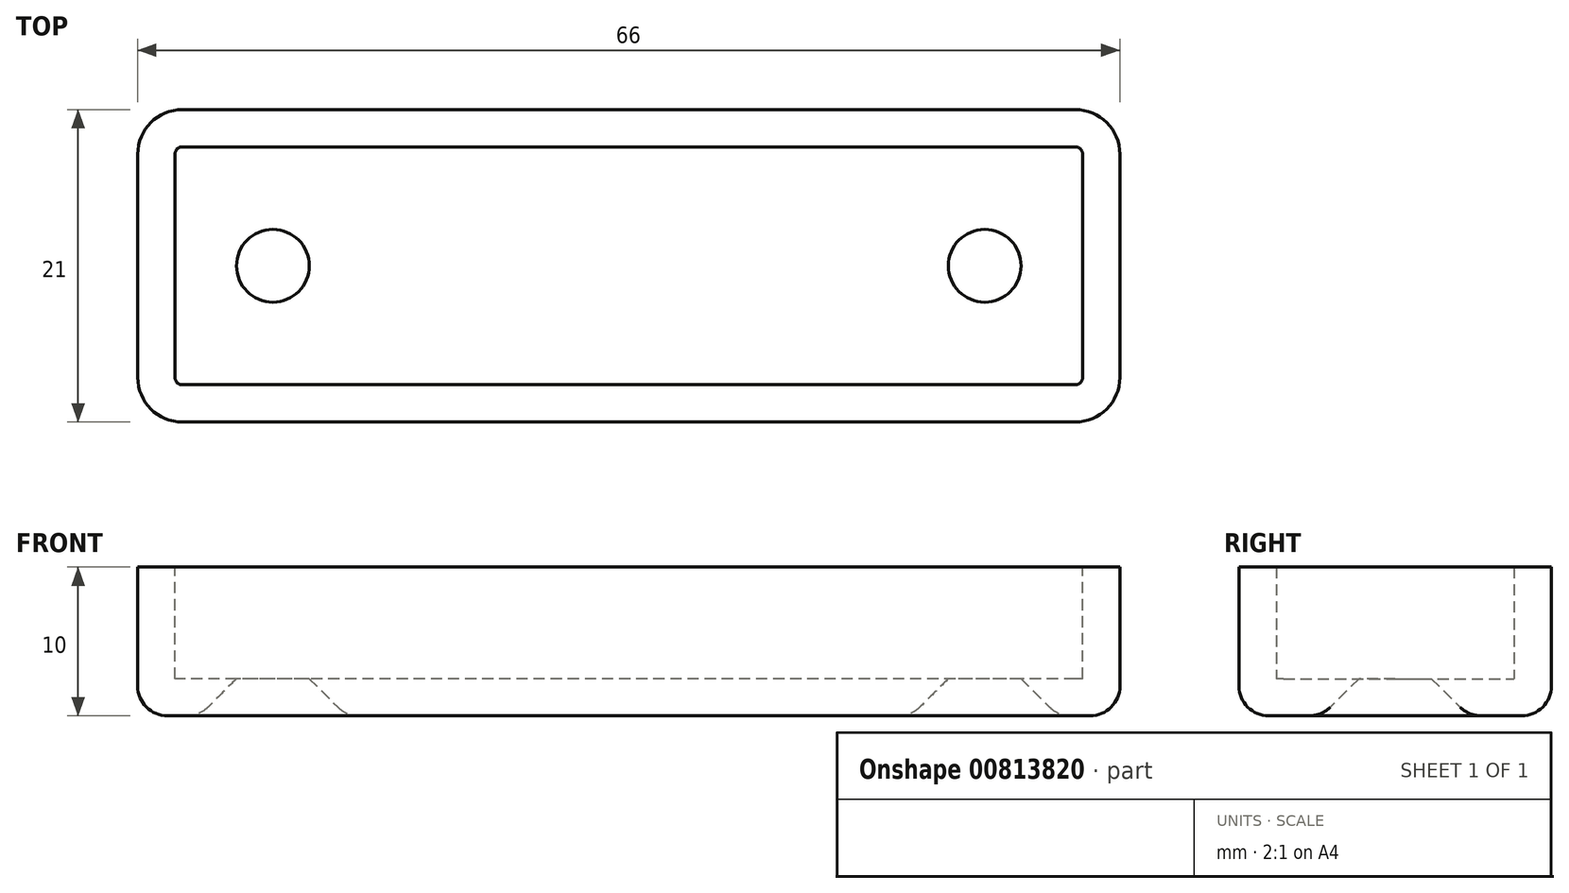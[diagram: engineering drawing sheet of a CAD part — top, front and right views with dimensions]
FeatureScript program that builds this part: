
annotation { "Feature Type Name" : "Feature", "Feature Type Description" : "" }
export const myFeature = defineFeature(function(context is Context, id is Id, definition is map)
    precondition{}
    {
        {
            var Q0;
            Q0=qCreatedBy(makeId("Top.planeOp"),FACE);
            var sketch = newSketch(context, id + "F0", { "sketchPlane" : qUnion([Q0])});
            skLineSegment(sketch, "E0.bottom", {"start": v(30, -10.5) * mm, "end": v(-30, -10.5) * mm});
            skLineSegment(sketch, "E0.top", {"start": v(30, 10.5) * mm, "end": v(-30, 10.5) * mm});
            skLineSegment(sketch, "E0.left", {"start": v(33, -7.5) * mm, "end": v(33, 7.5) * mm});
            skLineSegment(sketch, "E0.right", {"start": v(-33, -7.5) * mm, "end": v(-33, 7.5) * mm});
            skPoint(sketch, "E0.middle", {"position": v(0, 0) * mm});
            skPoint(sketch, "E1.visualSharp", {"position": v(-33, 10.5) * mm});
            skArc(sketch, "E1.filletArc", {"start": v(-30, 10.5) * mm, "mid": v(-32.12, 9.62) * mm, "end": v(-33, 7.5) * mm});
            skPoint(sketch, "E2.visualSharp", {"position": v(33, 10.5) * mm});
            skArc(sketch, "E2.filletArc", {"start": v(33, 7.5) * mm, "mid": v(32.12, 9.62) * mm, "end": v(30, 10.5) * mm});
            skPoint(sketch, "E3.visualSharp", {"position": v(33, -10.5) * mm});
            skArc(sketch, "E3.filletArc", {"start": v(30, -10.5) * mm, "mid": v(32.12, -9.62) * mm, "end": v(33, -7.5) * mm});
            skPoint(sketch, "E4.visualSharp", {"position": v(-33, -10.5) * mm});
            skArc(sketch, "E4.filletArc", {"start": v(-33, -7.5) * mm, "mid": v(-32.12, -9.62) * mm, "end": v(-30, -10.5) * mm});
            skSolve(sketch);
        }
        {
            var Q0;
            Q0 = qSketchRegion(id + "F0", true);
            extrude(context, id + "F1", {"entities" : qUnion([Q0]), "depth" : 10 * mm, "offsetDistance" : 25 * mm});
        }
        {
            var Q0;
            Q0=makeQuery(id+"F1.opExtrude","CAP_FACE",FACE,{"disambiguationData":[OSD([sQuery(id+"F0.wireOp",EDGE,"E0.bottom"),sQuery(id+"F0.wireOp",EDGE,"E0.top"),sQuery(id+"F0.wireOp",EDGE,"E0.left"),sQuery(id+"F0.wireOp",EDGE,"E0.right"),sQuery(id+"F0.wireOp",EDGE,"E1.filletArc"),sQuery(id+"F0.wireOp",EDGE,"E2.filletArc"),sQuery(id+"F0.wireOp",EDGE,"E3.filletArc"),sQuery(id+"F0.wireOp",EDGE,"E4.filletArc")])],"isStart":false});
            shell(context, id + "F2", {"entities" : qUnion([Q0]), "thickness" : 2.5 * mm});
        }
        {
            var Q0;
            Q0=makeQuery(id+"F2.opShell","OFFSET_FACE",FACE,{"disambiguationData":[OSD([sQuery(id+"F0.wireOp",EDGE,"E0.bottom"),sQuery(id+"F0.wireOp",EDGE,"E0.top"),sQuery(id+"F0.wireOp",EDGE,"E0.left"),sQuery(id+"F0.wireOp",EDGE,"E0.right"),sQuery(id+"F0.wireOp",EDGE,"E1.filletArc"),sQuery(id+"F0.wireOp",EDGE,"E2.filletArc"),sQuery(id+"F0.wireOp",EDGE,"E3.filletArc"),sQuery(id+"F0.wireOp",EDGE,"E4.filletArc")])]});
            var sketch = newSketch(context, id + "F3", { "sketchPlane" : qUnion([Q0])});
            skCircle(sketch, "E5", {"center": v(-23.92, 0) * mm, "radius": 1.95 * mm});
            skCircle(sketch, "E6.MirrorC", {"center": v(23.92, 0) * mm, "radius": 1.95 * mm});
            skSolve(sketch);
        }
        {
            var Q0;
            Q0 = qSketchRegion(id + "F3", true);
            extrude(context, id + "F4", {"entities" : qUnion([Q0]), "operationType" : NewBodyOperationType.REMOVE, "endBound" : BoundingType.THROUGH_ALL, "oppositeDirection" : true, "depth" : 25 * mm, "offsetDistance" : 25 * mm});
        }
        {
            var Q0;
            Q0=makeQuery(id+"F4.boolean.opBoolean","INTERSECT",EDGE,{"derivedFrom":[makeQuery(id+"F1.opExtrude","CAP_FACE",FACE,{"disambiguationData":[OSD([sQuery(id+"F0.wireOp",EDGE,"E0.bottom"),sQuery(id+"F0.wireOp",EDGE,"E0.top"),sQuery(id+"F0.wireOp",EDGE,"E0.left"),sQuery(id+"F0.wireOp",EDGE,"E0.right"),sQuery(id+"F0.wireOp",EDGE,"E1.filletArc"),sQuery(id+"F0.wireOp",EDGE,"E2.filletArc"),sQuery(id+"F0.wireOp",EDGE,"E3.filletArc"),sQuery(id+"F0.wireOp",EDGE,"E4.filletArc")])],"isStart":true}),makeQuery(id+"F4.opExtrude","SWEPT_FACE",FACE,{"disambiguationData":[OSD([sQuery(id+"F3.wireOp",EDGE,"E6.MirrorC")])]})]});
            var Q1;
            Q1=makeQuery(id+"F4.boolean.opBoolean","INTERSECT",EDGE,{"derivedFrom":[makeQuery(id+"F1.opExtrude","CAP_FACE",FACE,{"disambiguationData":[OSD([sQuery(id+"F0.wireOp",EDGE,"E0.bottom"),sQuery(id+"F0.wireOp",EDGE,"E0.top"),sQuery(id+"F0.wireOp",EDGE,"E0.left"),sQuery(id+"F0.wireOp",EDGE,"E0.right"),sQuery(id+"F0.wireOp",EDGE,"E1.filletArc"),sQuery(id+"F0.wireOp",EDGE,"E2.filletArc"),sQuery(id+"F0.wireOp",EDGE,"E3.filletArc"),sQuery(id+"F0.wireOp",EDGE,"E4.filletArc")])],"isStart":true}),makeQuery(id+"F4.opExtrude","SWEPT_FACE",FACE,{"disambiguationData":[OSD([sQuery(id+"F3.wireOp",EDGE,"E5")])]})]});
            chamfer(context, id + "F5", {"entities" : qUnion([Q0, Q1]), "width" : 3 * mm, "tangentPropagation" : true});
        }
        {
            var Q0;
            Q0=makeQuery(id+"F1.opExtrude","CAP_FACE",FACE,{"disambiguationData":[OSD([sQuery(id+"F0.wireOp",EDGE,"E0.bottom"),sQuery(id+"F0.wireOp",EDGE,"E0.top"),sQuery(id+"F0.wireOp",EDGE,"E0.left"),sQuery(id+"F0.wireOp",EDGE,"E0.right"),sQuery(id+"F0.wireOp",EDGE,"E1.filletArc"),sQuery(id+"F0.wireOp",EDGE,"E2.filletArc"),sQuery(id+"F0.wireOp",EDGE,"E3.filletArc"),sQuery(id+"F0.wireOp",EDGE,"E4.filletArc")])],"isStart":true});
            fillet(context, id + "F6", {"entities" : qUnion([Q0]), "radius" : 2 * mm, "tangentPropagation" : true, "allowEdgeOverflow" : false});
        }
    });
